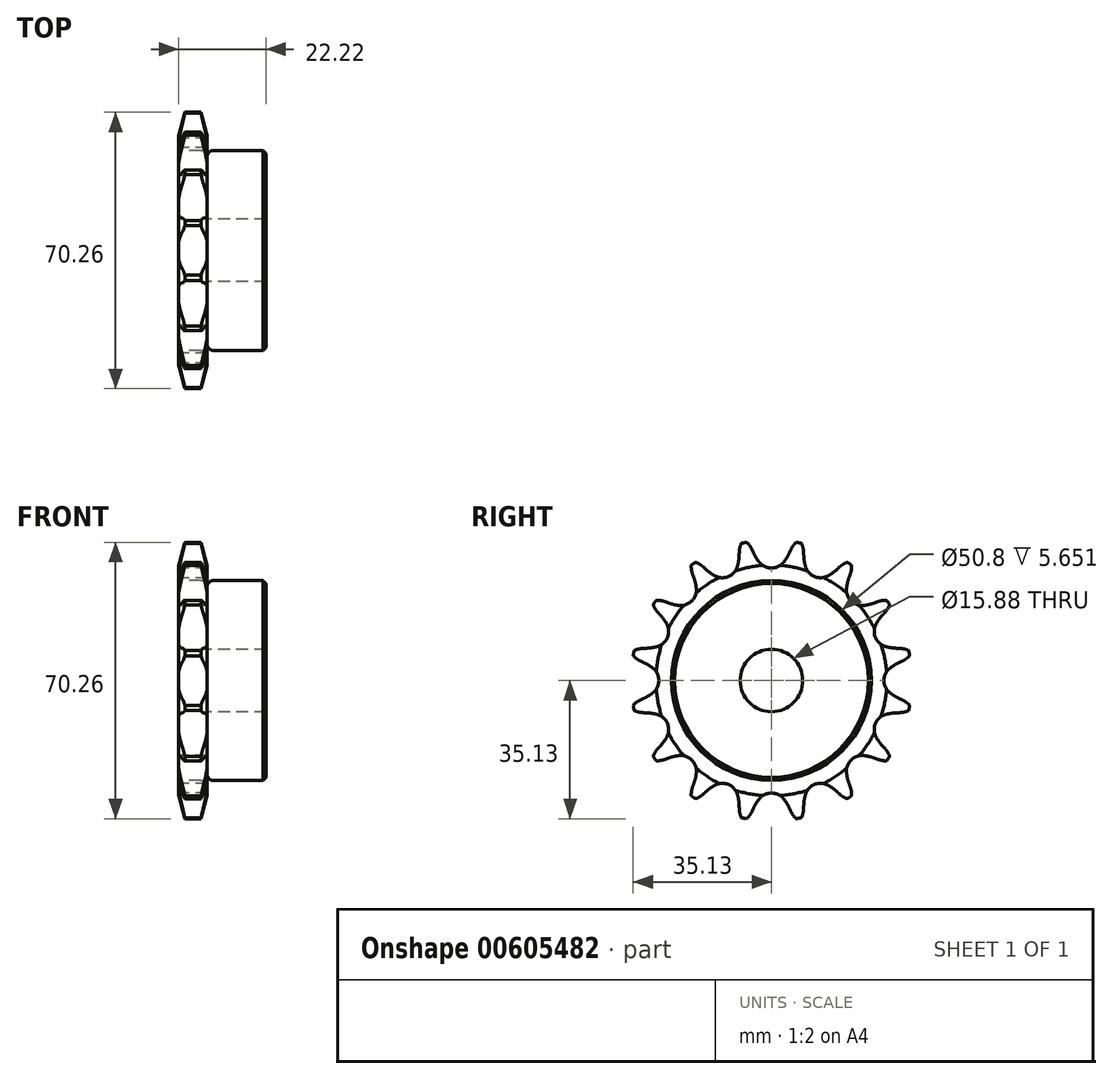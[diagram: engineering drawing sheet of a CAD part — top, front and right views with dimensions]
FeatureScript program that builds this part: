
annotation { "Feature Type Name" : "Feature", "Feature Type Description" : "" }
export const myFeature = defineFeature(function(context is Context, id is Id, definition is map)
    precondition{}
    {
        {
            var Q0;
            Q0=qCreatedBy(makeId("Front.planeOp"),FACE);
            var sketch = newSketch(context, id + "F0", { "sketchPlane" : qUnion([Q0])});
            skLineSegment(sketch, "E0", {"start": v(-23.98, 0) * mm, "end": v(-1.76, 0) * mm, "construction": true});
            skLineSegment(sketch, "E1.bottom", {"start": v(-23.98, 7.94) * mm, "end": v(-16.74, 7.94) * mm});
            skLineSegment(sketch, "E1.top", {"start": v(-23.98, 35.69) * mm, "end": v(-16.74, 35.69) * mm});
            skLineSegment(sketch, "E1.left", {"start": v(-23.98, 7.94) * mm, "end": v(-23.98, 35.69) * mm});
            skLineSegment(sketch, "E1.right", {"start": v(-16.74, 7.94) * mm, "end": v(-16.74, 35.69) * mm});
            skLineSegment(sketch, "E2.bottom", {"start": v(-23.98, 7.94) * mm, "end": v(-1.76, 7.94) * mm});
            skLineSegment(sketch, "E2.top", {"start": v(-23.98, 25.4) * mm, "end": v(-1.76, 25.4) * mm});
            skLineSegment(sketch, "E2.left", {"start": v(-23.98, 7.94) * mm, "end": v(-23.98, 25.4) * mm});
            skLineSegment(sketch, "E2.right", {"start": v(-1.76, 7.94) * mm, "end": v(-1.76, 25.4) * mm});
            skLineSegment(sketch, "E3.MirrorCS", {"start": v(-23.98, -25.4) * mm, "end": v(-1.76, -25.4) * mm});
            skLineSegment(sketch, "E4.MirrorCS", {"start": v(-23.98, -7.94) * mm, "end": v(-1.76, -7.94) * mm});
            skLineSegment(sketch, "E5.MirrorCS", {"start": v(-1.76, -7.94) * mm, "end": v(-1.76, -25.4) * mm});
            skLineSegment(sketch, "E6.MirrorCS", {"start": v(-16.74, -7.94) * mm, "end": v(-16.74, -35.69) * mm});
            skLineSegment(sketch, "E7.MirrorCS", {"start": v(-23.98, -7.94) * mm, "end": v(-23.98, -25.4) * mm});
            skLineSegment(sketch, "E8.MirrorCS", {"start": v(-23.98, -7.94) * mm, "end": v(-23.98, -35.69) * mm});
            skLineSegment(sketch, "E9.MirrorCS", {"start": v(-23.98, -35.69) * mm, "end": v(-16.74, -35.69) * mm});
            skSolve(sketch);
        }
        {
            var Q0;
            {var subQ0=sQuery(id+"F0.wireOp",EDGE,"E1.top");Q0=makeQuery(id+"F0.imprint","IMPRINT",FACE,{"disambiguationData":[TD([[makeQuery(id+"F0.imprint","IMPRINT",EDGE,{"derivedFrom":subQ0}),-1.0]])]});}
            var Q1;
            {var subQ5=sQuery(id+"F0.wireOp",EDGE,"E2.left");Q1=makeQuery(id+"F0.imprint","IMPRINT",FACE,{"disambiguationData":[TD([[makeQuery(id+"F0.imprint","IMPRINT",EDGE,{"derivedFrom":subQ5}),-1.0]])]});}
            var Q2;
            {var subQ5=sQuery(id+"F0.wireOp",EDGE,"E2.right");Q2=makeQuery(id+"F0.imprint","IMPRINT",FACE,{"disambiguationData":[TD([[makeQuery(id+"F0.imprint","IMPRINT",EDGE,{"derivedFrom":subQ5}),1.0]])]});}
            var Q3;
            Q3=sQuery(id+"F0.wireOp",EDGE,"E0");
            revolve(context, id + "F1", {"entities" : qUnion([Q0, Q1, Q2]), "axis" : qUnion([Q3]), "revolveType" : RevolveType.FULL});
        }
        {
            var Q0;
            Q0=makeQuery(id+"F1.opRevolve","SWEPT_EDGE",EDGE,{"disambiguationData":[OSD([sQuery(id+"F0.wireOp",EDGE,"E1.right"),sQuery(id+"F0.wireOp",EDGE,"E2.top")])]});
            fillet(context, id + "F2", {"entities" : qUnion([Q0]), "radius" : 1.59 * mm, "tangentPropagation" : true, "allowEdgeOverflow" : false});
        }
        {
            var Q0;
            Q0=makeQuery(id+"F1.opRevolve","SWEPT_EDGE",EDGE,{"disambiguationData":[OSD([sQuery(id+"F0.wireOp",EDGE,"E2.top"),sQuery(id+"F0.wireOp",EDGE,"E2.right")])]});
            chamfer(context, id + "F3", {"entities" : qUnion([Q0]), "width" : 0.8 * mm, "tangentPropagation" : true});
        }
        {
            var Q0;
            Q0=makeQuery(id+"F1.opRevolve","SWEPT_EDGE",EDGE,{"disambiguationData":[OSD([sQuery(id+"F0.wireOp",EDGE,"E1.top"),sQuery(id+"F0.wireOp",EDGE,"E1.right")])]});
            var Q1;
            Q1=makeQuery(id+"F1.opRevolve","SWEPT_EDGE",EDGE,{"disambiguationData":[OSD([sQuery(id+"F0.wireOp",EDGE,"E1.top"),sQuery(id+"F0.wireOp",EDGE,"E1.left")])]});
            chamfer(context, id + "F4", {"entities" : qUnion([Q0, Q1]), "chamferType" : ChamferType.TWO_OFFSETS, "width1" : 1.57 * mm, "oppositeDirection" : false, "width2" : 6.35 * mm, "tangentPropagation" : true});
        }
        {
            var Q0;
            Q0=makeQuery(id+"F1.opRevolve","SWEPT_FACE",FACE,{"disambiguationData":[OSD([sQuery(id+"F0.wireOp",EDGE,"E1.left"),sQuery(id+"F0.wireOp",EDGE,"E2.left")])]});
            var sketch = newSketch(context, id + "F5", { "sketchPlane" : qUnion([Q0])});
            skCircle(sketch, "E10", {"center": v(0, 0) * mm, "radius": 32.55 * mm, "construction": true});
            skLineSegment(sketch, "E11", {"start": v(0, 0) * mm, "end": v(0, 32.55) * mm, "construction": true});
            skLineSegment(sketch, "E12", {"start": v(0, 32.55) * mm, "end": v(5.9, 37.28) * mm, "construction": true});
            skLineSegment(sketch, "E13", {"start": v(5.9, 37.28) * mm, "end": v(-4.61, 32.55) * mm, "construction": true});
            skLineSegment(sketch, "E14", {"start": v(-4.61, 32.55) * mm, "end": v(-4.86, 33.1) * mm});
            skLineSegment(sketch, "E15", {"start": v(0, 32.55) * mm, "end": v(48.05, 32.55) * mm, "construction": true});
            skLineSegment(sketch, "E16", {"start": v(0, 0) * mm, "end": v(-7.12, 35.82) * mm, "construction": true});
            skLineSegment(sketch, "E17", {"start": v(-7.12, 35.82) * mm, "end": v(-7.12, 35.82) * mm});
            skArc(sketch, "E18", {"start": v(-4.86, 33.1) * mm, "mid": v(-5.8, 34.61) * mm, "end": v(-7.12, 35.82) * mm});
            skArc(sketch, "E19", {"start": v(-7.12, 35.82) * mm, "mid": v(-15.93, 26.17) * mm, "end": v(-4.86, 33.1) * mm, "construction": true});
            skLineSegment(sketch, "E20", {"start": v(-4.61, 32.55) * mm, "end": v(-4.61, 32.55) * mm});
            skArc(sketch, "E21", {"start": v(-4.61, 32.55) * mm, "mid": v(-3.93, 31.26) * mm, "end": v(-3.1, 30.07) * mm});
            skArc(sketch, "E22", {"start": v(-3.1, 30.07) * mm, "mid": v(15.72, 43.3) * mm, "end": v(-4.61, 32.55) * mm, "construction": true});
            skArc(sketch, "E23.MirrorCS", {"start": v(7.12, 35.82) * mm, "mid": v(15.93, 26.17) * mm, "end": v(4.86, 33.1) * mm, "construction": true});
            skArc(sketch, "E24.MirrorCS", {"start": v(3.1, 30.07) * mm, "mid": v(-15.72, 43.3) * mm, "end": v(4.61, 32.55) * mm, "construction": true});
            skArc(sketch, "E25.MirrorCS", {"start": v(4.61, 32.55) * mm, "mid": v(3.93, 31.26) * mm, "end": v(3.1, 30.07) * mm});
            skLineSegment(sketch, "E26.MirrorCS", {"start": v(4.61, 32.55) * mm, "end": v(4.86, 33.1) * mm});
            skArc(sketch, "E27.MirrorCS", {"start": v(4.86, 33.1) * mm, "mid": v(5.8, 34.61) * mm, "end": v(7.12, 35.82) * mm});
            skArc(sketch, "E28", {"start": v(3.1, 30.07) * mm, "mid": v(0, 28.59) * mm, "end": v(-3.1, 30.07) * mm});
            skLineSegment(sketch, "E29", {"start": v(-4.86, 33.1) * mm, "end": v(-4.61, 32.55) * mm});
            skLineSegment(sketch, "E30.1.0", {"start": v(-17.15, 28.72) * mm, "end": v(-16.72, 28.3) * mm});
            skArc(sketch, "E30.1.1", {"start": v(-17.15, 28.72) * mm, "mid": v(-18.6, 29.76) * mm, "end": v(-20.29, 30.36) * mm});
            skArc(sketch, "E30.1.2", {"start": v(-16.72, 28.3) * mm, "mid": v(-15.6, 27.38) * mm, "end": v(-14.36, 26.6) * mm});
            skArc(sketch, "E30.1.3", {"start": v(-8.65, 28.96) * mm, "mid": v(-10.94, 26.41) * mm, "end": v(-14.36, 26.6) * mm});
            skArc(sketch, "E30.1.4", {"start": v(-8.2, 31.84) * mm, "mid": v(-8.33, 30.39) * mm, "end": v(-8.65, 28.96) * mm});
            skLineSegment(sketch, "E30.1.5", {"start": v(-8.2, 31.84) * mm, "end": v(-8.18, 32.44) * mm});
            skArc(sketch, "E30.1.6", {"start": v(-8.18, 32.44) * mm, "mid": v(-7.88, 34.2) * mm, "end": v(-7.12, 35.82) * mm});
            skLineSegment(sketch, "E30.2.0", {"start": v(-26.84, 19.97) * mm, "end": v(-26.28, 19.76) * mm});
            skArc(sketch, "E30.2.1", {"start": v(-26.84, 19.97) * mm, "mid": v(-28.58, 20.37) * mm, "end": v(-30.36, 20.29) * mm});
            skArc(sketch, "E30.2.2", {"start": v(-26.28, 19.76) * mm, "mid": v(-24.88, 19.33) * mm, "end": v(-23.45, 19.08) * mm});
            skArc(sketch, "E30.2.3", {"start": v(-19.08, 23.45) * mm, "mid": v(-20.21, 20.21) * mm, "end": v(-23.45, 19.08) * mm});
            skArc(sketch, "E30.2.4", {"start": v(-19.76, 26.28) * mm, "mid": v(-19.33, 24.88) * mm, "end": v(-19.08, 23.45) * mm});
            skLineSegment(sketch, "E30.2.5", {"start": v(-19.76, 26.28) * mm, "end": v(-19.97, 26.84) * mm});
            skArc(sketch, "E30.2.6", {"start": v(-19.97, 26.84) * mm, "mid": v(-20.37, 28.58) * mm, "end": v(-20.29, 30.36) * mm});
            skLineSegment(sketch, "E30.3.0", {"start": v(-32.44, 8.18) * mm, "end": v(-31.84, 8.2) * mm});
            skArc(sketch, "E30.3.1", {"start": v(-32.44, 8.18) * mm, "mid": v(-34.2, 7.88) * mm, "end": v(-35.82, 7.12) * mm});
            skArc(sketch, "E30.3.2", {"start": v(-31.84, 8.2) * mm, "mid": v(-30.39, 8.33) * mm, "end": v(-28.96, 8.65) * mm});
            skArc(sketch, "E30.3.3", {"start": v(-26.6, 14.36) * mm, "mid": v(-26.41, 10.94) * mm, "end": v(-28.96, 8.65) * mm});
            skArc(sketch, "E30.3.4", {"start": v(-28.3, 16.72) * mm, "mid": v(-27.38, 15.6) * mm, "end": v(-26.6, 14.36) * mm});
            skLineSegment(sketch, "E30.3.5", {"start": v(-28.3, 16.72) * mm, "end": v(-28.72, 17.15) * mm});
            skArc(sketch, "E30.3.6", {"start": v(-28.72, 17.15) * mm, "mid": v(-29.76, 18.6) * mm, "end": v(-30.36, 20.29) * mm});
            skLineSegment(sketch, "E30.4.0", {"start": v(-33.1, -4.86) * mm, "end": v(-32.55, -4.61) * mm});
            skArc(sketch, "E30.4.1", {"start": v(-33.1, -4.86) * mm, "mid": v(-34.61, -5.8) * mm, "end": v(-35.82, -7.12) * mm});
            skArc(sketch, "E30.4.2", {"start": v(-32.55, -4.61) * mm, "mid": v(-31.26, -3.93) * mm, "end": v(-30.07, -3.1) * mm});
            skArc(sketch, "E30.4.3", {"start": v(-30.07, 3.1) * mm, "mid": v(-28.59, 0) * mm, "end": v(-30.07, -3.1) * mm});
            skArc(sketch, "E30.4.4", {"start": v(-32.55, 4.61) * mm, "mid": v(-31.26, 3.93) * mm, "end": v(-30.07, 3.1) * mm});
            skLineSegment(sketch, "E30.4.5", {"start": v(-32.55, 4.61) * mm, "end": v(-33.1, 4.86) * mm});
            skArc(sketch, "E30.4.6", {"start": v(-33.1, 4.86) * mm, "mid": v(-34.61, 5.8) * mm, "end": v(-35.82, 7.12) * mm});
            skLineSegment(sketch, "E30.5.0", {"start": v(-28.72, -17.15) * mm, "end": v(-28.3, -16.72) * mm});
            skArc(sketch, "E30.5.1", {"start": v(-28.72, -17.15) * mm, "mid": v(-29.76, -18.6) * mm, "end": v(-30.36, -20.29) * mm});
            skArc(sketch, "E30.5.2", {"start": v(-28.3, -16.72) * mm, "mid": v(-27.38, -15.6) * mm, "end": v(-26.6, -14.36) * mm});
            skArc(sketch, "E30.5.3", {"start": v(-28.96, -8.65) * mm, "mid": v(-26.41, -10.94) * mm, "end": v(-26.6, -14.36) * mm});
            skArc(sketch, "E30.5.4", {"start": v(-31.84, -8.2) * mm, "mid": v(-30.39, -8.33) * mm, "end": v(-28.96, -8.65) * mm});
            skLineSegment(sketch, "E30.5.5", {"start": v(-31.84, -8.2) * mm, "end": v(-32.44, -8.18) * mm});
            skArc(sketch, "E30.5.6", {"start": v(-32.44, -8.18) * mm, "mid": v(-34.2, -7.88) * mm, "end": v(-35.82, -7.12) * mm});
            skLineSegment(sketch, "E30.6.0", {"start": v(-19.97, -26.84) * mm, "end": v(-19.76, -26.28) * mm});
            skArc(sketch, "E30.6.1", {"start": v(-19.97, -26.84) * mm, "mid": v(-20.37, -28.58) * mm, "end": v(-20.29, -30.36) * mm});
            skArc(sketch, "E30.6.2", {"start": v(-19.76, -26.28) * mm, "mid": v(-19.33, -24.88) * mm, "end": v(-19.08, -23.45) * mm});
            skArc(sketch, "E30.6.3", {"start": v(-23.45, -19.08) * mm, "mid": v(-20.21, -20.21) * mm, "end": v(-19.08, -23.45) * mm});
            skArc(sketch, "E30.6.4", {"start": v(-26.28, -19.76) * mm, "mid": v(-24.88, -19.33) * mm, "end": v(-23.45, -19.08) * mm});
            skLineSegment(sketch, "E30.6.5", {"start": v(-26.28, -19.76) * mm, "end": v(-26.84, -19.97) * mm});
            skArc(sketch, "E30.6.6", {"start": v(-26.84, -19.97) * mm, "mid": v(-28.58, -20.37) * mm, "end": v(-30.36, -20.29) * mm});
            skLineSegment(sketch, "E30.7.0", {"start": v(-8.18, -32.44) * mm, "end": v(-8.2, -31.84) * mm});
            skArc(sketch, "E30.7.1", {"start": v(-8.18, -32.44) * mm, "mid": v(-7.88, -34.2) * mm, "end": v(-7.12, -35.82) * mm});
            skArc(sketch, "E30.7.2", {"start": v(-8.2, -31.84) * mm, "mid": v(-8.33, -30.39) * mm, "end": v(-8.65, -28.96) * mm});
            skArc(sketch, "E30.7.3", {"start": v(-14.36, -26.6) * mm, "mid": v(-10.94, -26.41) * mm, "end": v(-8.65, -28.96) * mm});
            skArc(sketch, "E30.7.4", {"start": v(-16.72, -28.3) * mm, "mid": v(-15.6, -27.38) * mm, "end": v(-14.36, -26.6) * mm});
            skLineSegment(sketch, "E30.7.5", {"start": v(-16.72, -28.3) * mm, "end": v(-17.15, -28.72) * mm});
            skArc(sketch, "E30.7.6", {"start": v(-17.15, -28.72) * mm, "mid": v(-18.6, -29.76) * mm, "end": v(-20.29, -30.36) * mm});
            skLineSegment(sketch, "E30.8.0", {"start": v(4.86, -33.1) * mm, "end": v(4.61, -32.55) * mm});
            skArc(sketch, "E30.8.1", {"start": v(4.86, -33.1) * mm, "mid": v(5.8, -34.61) * mm, "end": v(7.12, -35.82) * mm});
            skArc(sketch, "E30.8.2", {"start": v(4.61, -32.55) * mm, "mid": v(3.93, -31.26) * mm, "end": v(3.1, -30.07) * mm});
            skArc(sketch, "E30.8.3", {"start": v(-3.1, -30.07) * mm, "mid": v(0, -28.59) * mm, "end": v(3.1, -30.07) * mm});
            skArc(sketch, "E30.8.4", {"start": v(-4.61, -32.55) * mm, "mid": v(-3.93, -31.26) * mm, "end": v(-3.1, -30.07) * mm});
            skLineSegment(sketch, "E30.8.5", {"start": v(-4.61, -32.55) * mm, "end": v(-4.86, -33.1) * mm});
            skArc(sketch, "E30.8.6", {"start": v(-4.86, -33.1) * mm, "mid": v(-5.8, -34.61) * mm, "end": v(-7.12, -35.82) * mm});
            skLineSegment(sketch, "E30.9.0", {"start": v(17.15, -28.72) * mm, "end": v(16.72, -28.3) * mm});
            skArc(sketch, "E30.9.1", {"start": v(17.15, -28.72) * mm, "mid": v(18.6, -29.76) * mm, "end": v(20.29, -30.36) * mm});
            skArc(sketch, "E30.9.2", {"start": v(16.72, -28.3) * mm, "mid": v(15.6, -27.38) * mm, "end": v(14.36, -26.6) * mm});
            skArc(sketch, "E30.9.3", {"start": v(8.65, -28.96) * mm, "mid": v(10.94, -26.41) * mm, "end": v(14.36, -26.6) * mm});
            skArc(sketch, "E30.9.4", {"start": v(8.2, -31.84) * mm, "mid": v(8.33, -30.39) * mm, "end": v(8.65, -28.96) * mm});
            skLineSegment(sketch, "E30.9.5", {"start": v(8.2, -31.84) * mm, "end": v(8.18, -32.44) * mm});
            skArc(sketch, "E30.9.6", {"start": v(8.18, -32.44) * mm, "mid": v(7.88, -34.2) * mm, "end": v(7.12, -35.82) * mm});
            skLineSegment(sketch, "E30.10.0", {"start": v(26.84, -19.97) * mm, "end": v(26.28, -19.76) * mm});
            skArc(sketch, "E30.10.1", {"start": v(26.84, -19.97) * mm, "mid": v(28.58, -20.37) * mm, "end": v(30.36, -20.29) * mm});
            skArc(sketch, "E30.10.2", {"start": v(26.28, -19.76) * mm, "mid": v(24.88, -19.33) * mm, "end": v(23.45, -19.08) * mm});
            skArc(sketch, "E30.10.3", {"start": v(19.08, -23.45) * mm, "mid": v(20.21, -20.21) * mm, "end": v(23.45, -19.08) * mm});
            skArc(sketch, "E30.10.4", {"start": v(19.76, -26.28) * mm, "mid": v(19.33, -24.88) * mm, "end": v(19.08, -23.45) * mm});
            skLineSegment(sketch, "E30.10.5", {"start": v(19.76, -26.28) * mm, "end": v(19.97, -26.84) * mm});
            skArc(sketch, "E30.10.6", {"start": v(19.97, -26.84) * mm, "mid": v(20.37, -28.58) * mm, "end": v(20.29, -30.36) * mm});
            skLineSegment(sketch, "E30.11.0", {"start": v(32.44, -8.18) * mm, "end": v(31.84, -8.2) * mm});
            skArc(sketch, "E30.11.1", {"start": v(32.44, -8.18) * mm, "mid": v(34.2, -7.88) * mm, "end": v(35.82, -7.12) * mm});
            skArc(sketch, "E30.11.2", {"start": v(31.84, -8.2) * mm, "mid": v(30.39, -8.33) * mm, "end": v(28.96, -8.65) * mm});
            skArc(sketch, "E30.11.3", {"start": v(26.6, -14.36) * mm, "mid": v(26.41, -10.94) * mm, "end": v(28.96, -8.65) * mm});
            skArc(sketch, "E30.11.4", {"start": v(28.3, -16.72) * mm, "mid": v(27.38, -15.6) * mm, "end": v(26.6, -14.36) * mm});
            skLineSegment(sketch, "E30.11.5", {"start": v(28.3, -16.72) * mm, "end": v(28.72, -17.15) * mm});
            skArc(sketch, "E30.11.6", {"start": v(28.72, -17.15) * mm, "mid": v(29.76, -18.6) * mm, "end": v(30.36, -20.29) * mm});
            skLineSegment(sketch, "E30.12.0", {"start": v(33.1, 4.86) * mm, "end": v(32.55, 4.61) * mm});
            skArc(sketch, "E30.12.1", {"start": v(33.1, 4.86) * mm, "mid": v(34.61, 5.8) * mm, "end": v(35.82, 7.12) * mm});
            skArc(sketch, "E30.12.2", {"start": v(32.55, 4.61) * mm, "mid": v(31.26, 3.93) * mm, "end": v(30.07, 3.1) * mm});
            skArc(sketch, "E30.12.3", {"start": v(30.07, -3.1) * mm, "mid": v(28.59, 0) * mm, "end": v(30.07, 3.1) * mm});
            skArc(sketch, "E30.12.4", {"start": v(32.55, -4.61) * mm, "mid": v(31.26, -3.93) * mm, "end": v(30.07, -3.1) * mm});
            skLineSegment(sketch, "E30.12.5", {"start": v(32.55, -4.61) * mm, "end": v(33.1, -4.86) * mm});
            skArc(sketch, "E30.12.6", {"start": v(33.1, -4.86) * mm, "mid": v(34.61, -5.8) * mm, "end": v(35.82, -7.12) * mm});
            skLineSegment(sketch, "E30.13.0", {"start": v(28.72, 17.15) * mm, "end": v(28.3, 16.72) * mm});
            skArc(sketch, "E30.13.1", {"start": v(28.72, 17.15) * mm, "mid": v(29.76, 18.6) * mm, "end": v(30.36, 20.29) * mm});
            skArc(sketch, "E30.13.2", {"start": v(28.3, 16.72) * mm, "mid": v(27.38, 15.6) * mm, "end": v(26.6, 14.36) * mm});
            skArc(sketch, "E30.13.3", {"start": v(28.96, 8.65) * mm, "mid": v(26.41, 10.94) * mm, "end": v(26.6, 14.36) * mm});
            skArc(sketch, "E30.13.4", {"start": v(31.84, 8.2) * mm, "mid": v(30.39, 8.33) * mm, "end": v(28.96, 8.65) * mm});
            skLineSegment(sketch, "E30.13.5", {"start": v(31.84, 8.2) * mm, "end": v(32.44, 8.18) * mm});
            skArc(sketch, "E30.13.6", {"start": v(32.44, 8.18) * mm, "mid": v(34.2, 7.88) * mm, "end": v(35.82, 7.12) * mm});
            skLineSegment(sketch, "E30.14.0", {"start": v(19.97, 26.84) * mm, "end": v(19.76, 26.28) * mm});
            skArc(sketch, "E30.14.1", {"start": v(19.97, 26.84) * mm, "mid": v(20.37, 28.58) * mm, "end": v(20.29, 30.36) * mm});
            skArc(sketch, "E30.14.2", {"start": v(19.76, 26.28) * mm, "mid": v(19.33, 24.88) * mm, "end": v(19.08, 23.45) * mm});
            skArc(sketch, "E30.14.3", {"start": v(23.45, 19.08) * mm, "mid": v(20.21, 20.21) * mm, "end": v(19.08, 23.45) * mm});
            skArc(sketch, "E30.14.4", {"start": v(26.28, 19.76) * mm, "mid": v(24.88, 19.33) * mm, "end": v(23.45, 19.08) * mm});
            skLineSegment(sketch, "E30.14.5", {"start": v(26.28, 19.76) * mm, "end": v(26.84, 19.97) * mm});
            skArc(sketch, "E30.14.6", {"start": v(26.84, 19.97) * mm, "mid": v(28.58, 20.37) * mm, "end": v(30.36, 20.29) * mm});
            skLineSegment(sketch, "E30.15.0", {"start": v(8.18, 32.44) * mm, "end": v(8.2, 31.84) * mm});
            skArc(sketch, "E30.15.1", {"start": v(8.18, 32.44) * mm, "mid": v(7.88, 34.2) * mm, "end": v(7.12, 35.82) * mm});
            skArc(sketch, "E30.15.2", {"start": v(8.2, 31.84) * mm, "mid": v(8.33, 30.39) * mm, "end": v(8.65, 28.96) * mm});
            skArc(sketch, "E30.15.3", {"start": v(14.36, 26.6) * mm, "mid": v(10.94, 26.41) * mm, "end": v(8.65, 28.96) * mm});
            skArc(sketch, "E30.15.4", {"start": v(16.72, 28.3) * mm, "mid": v(15.6, 27.38) * mm, "end": v(14.36, 26.6) * mm});
            skLineSegment(sketch, "E30.15.5", {"start": v(16.72, 28.3) * mm, "end": v(17.15, 28.72) * mm});
            skArc(sketch, "E30.15.6", {"start": v(17.15, 28.72) * mm, "mid": v(18.6, 29.76) * mm, "end": v(20.29, 30.36) * mm});
            skSolve(sketch);
        }
        {
            var Q0;
            Q0 = qSketchRegion(id + "F5", true);
            extrude(context, id + "F6", {"entities" : qUnion([Q0]), "operationType" : NewBodyOperationType.INTERSECT, "oppositeDirection" : true, "depth" : 25.4 * mm, "offsetDistance" : 25.4 * mm});
        }
    });
